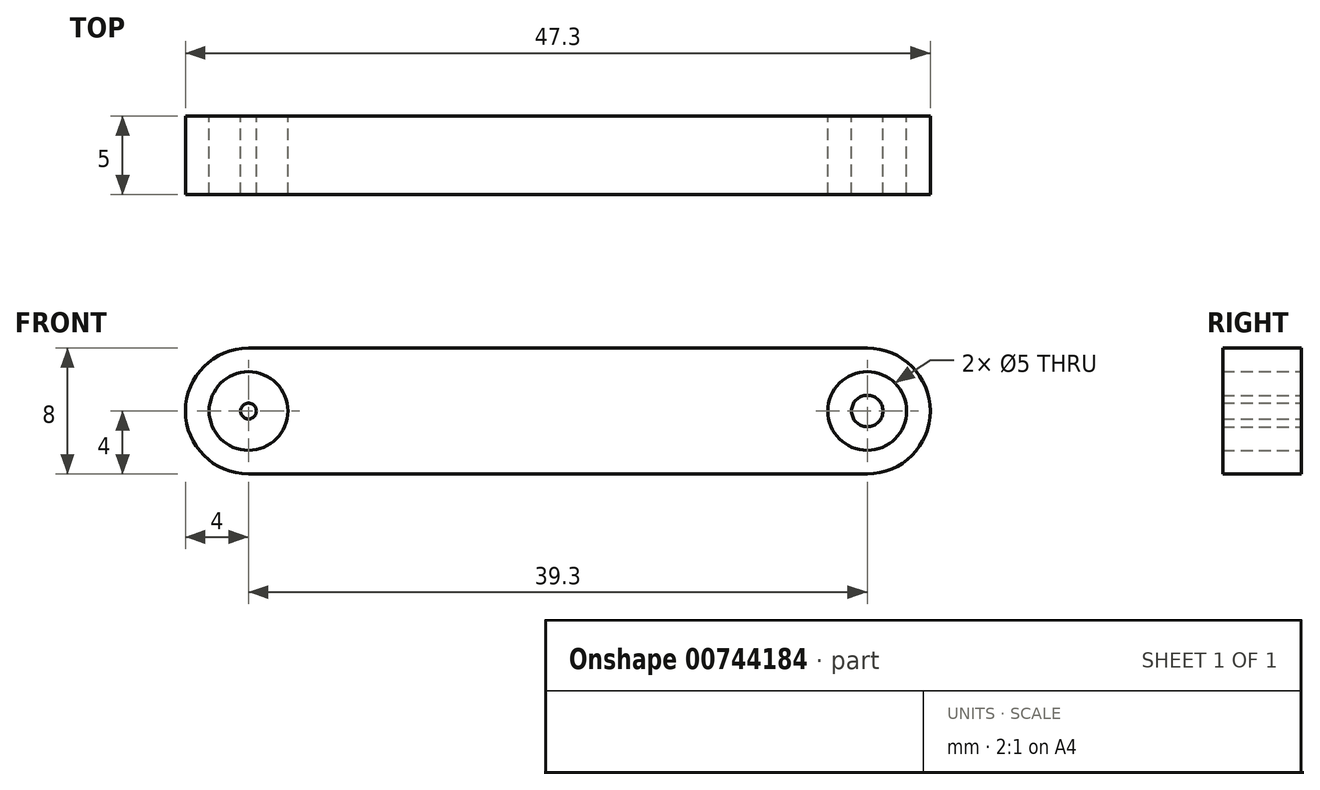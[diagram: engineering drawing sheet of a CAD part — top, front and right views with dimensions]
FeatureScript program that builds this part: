
annotation { "Feature Type Name" : "Feature", "Feature Type Description" : "" }
export const myFeature = defineFeature(function(context is Context, id is Id, definition is map)
    precondition{}
    {
        {
            var Q0;
            Q0=qCreatedBy(makeId("Front.planeOp"),FACE);
            var sketch = newSketch(context, id + "F0", { "sketchPlane" : qUnion([Q0])});
            skCircle(sketch, "E0", {"center": v(0, 0) * mm, "radius": 4 * mm});
            skCircle(sketch, "E1", {"center": v(39.3, 0) * mm, "radius": 4 * mm});
            skLineSegment(sketch, "E2", {"start": v(0, -4) * mm, "end": v(39.3, -4) * mm});
            skLineSegment(sketch, "E3", {"start": v(0, 4) * mm, "end": v(39.3, 4) * mm});
            skCircle(sketch, "E4", {"center": v(39.3, 0) * mm, "radius": 2.5 * mm});
            skCircle(sketch, "E5", {"center": v(0, 0) * mm, "radius": 2.5 * mm});
            skCircle(sketch, "E6", {"center": v(0, 0) * mm, "radius": 0.5 * mm});
            skCircle(sketch, "E7", {"center": v(39.3, 0) * mm, "radius": 1 * mm});
            skSolve(sketch);
        }
        {
            var Q0;
            Q0=qSketchRegion(id+"F0",true);
            var Q1;
            Q1=makeQuery(id+"F0.imprint","IMPRINT",FACE,{"disambiguationData":[TD([[makeQuery(id+"F0.imprint","IMPRINT",EDGE,{"derivedFrom":sQuery(id+"F0.wireOp",EDGE,"E6")}),1.0]])]});
            var Q2;
            Q2=makeQuery(id+"F0.imprint","IMPRINT",FACE,{"disambiguationData":[TD([[makeQuery(id+"F0.imprint","IMPRINT",EDGE,{"derivedFrom":sQuery(id+"F0.wireOp",EDGE,"E7")}),1.0]])]});
            extrude(context, id + "F1", {"entities" : qUnion([Q0, Q1, Q2]), "depth" : 5 * mm, "offsetDistance" : 25 * mm});
        }
    });
